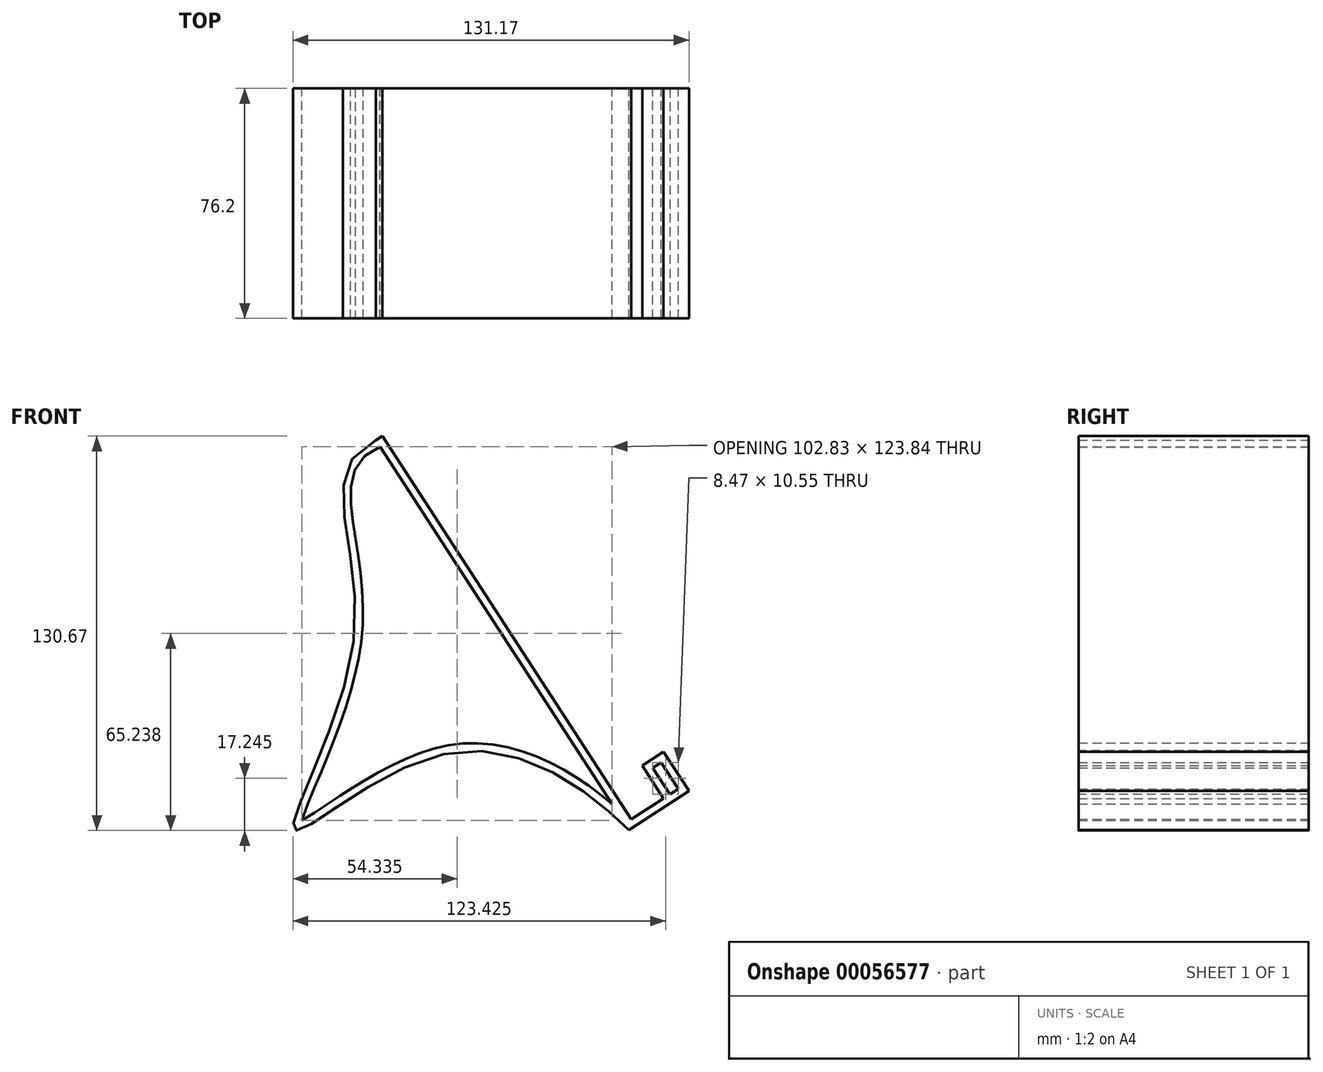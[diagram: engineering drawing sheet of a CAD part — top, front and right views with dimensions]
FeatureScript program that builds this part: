
annotation { "Feature Type Name" : "Feature", "Feature Type Description" : "" }
export const myFeature = defineFeature(function(context is Context, id is Id, definition is map)
    precondition{}
    {
        {
            var Q0;
            Q0=qCreatedBy(makeId("Front.planeOp"),FACE);
            var sketch = newSketch(context, id + "F0", { "sketchPlane" : qUnion([Q0])});
            skLineSegment(sketch, "E0.bottom", {"start": v(0, 0) * mm, "end": v(80.32, 0) * mm, "construction": true});
            skLineSegment(sketch, "E0.top", {"start": v(0, -127) * mm, "end": v(80.32, -127) * mm, "construction": true});
            skLineSegment(sketch, "E0.left", {"start": v(0, 0) * mm, "end": v(0, -127) * mm, "construction": true});
            skLineSegment(sketch, "E0.right", {"start": v(80.32, 0) * mm, "end": v(80.32, -127) * mm, "construction": true});
            skLineSegment(sketch, "E1", {"start": v(-12.8, 0) * mm, "end": v(69.67, -127) * mm});
            skLineSegment(sketch, "E2", {"start": v(69.67, -127) * mm, "end": v(80.32, -120.08) * mm});
            skLineSegment(sketch, "E3", {"start": v(80.32, -120.08) * mm, "end": v(73.27, -109.22) * mm});
            skLineSegment(sketch, "E4", {"start": v(-12.8, 0) * mm, "end": v(-14.93, -1.38) * mm});
            skLineSegment(sketch, "E5", {"start": v(-14.93, -1.38) * mm, "end": v(68.93, -130.51) * mm});
            skLineSegment(sketch, "E6", {"start": v(68.93, -130.51) * mm, "end": v(88.76, -117.63) * mm});
            skLineSegment(sketch, "E7", {"start": v(88.76, -117.63) * mm, "end": v(80.32, -104.64) * mm});
            skLineSegment(sketch, "E8", {"start": v(80.32, -104.64) * mm, "end": v(73.27, -109.22) * mm});
            skPoint(sketch, "E9.3.internal.snap0", {"position": v(0, -63.5) * mm});
            skFitSpline(sketch, "E9", {"points": [v(68.93, -130.51) * mm, v(10.64, -104.78) * mm, v(-41.93, -130.51) * mm, v(-21.9, -63.5) * mm, v(-14.93, -1.38) * mm], "startDerivative": vector(-127.8, 127.82) * mm, "endDerivative": vector(251.96, 110.75) * mm});
            skSolve(sketch);
        }
        {
            var Q0;
            Q0=makeQuery(id+"F0.imprint","IMPRINT",FACE,{"disambiguationData":[TD([[makeQuery(id+"F0.imprint","IMPRINT",EDGE,{"derivedFrom":sQuery(id+"F0.wireOp",EDGE,"E1")}),-1.0]])]});
            var Q1;
            Q1=makeQuery(id+"F0.imprint","IMPRINT",FACE,{"disambiguationData":[TD([[makeQuery(id+"F0.imprint","IMPRINT",EDGE,{"derivedFrom":sQuery(id+"F0.wireOp",EDGE,"E5")}),-1.0]])]});
            extrude(context, id + "F1", {"entities" : qUnion([Q0, Q1]), "depth" : 76.2 * mm});
        }
        {
            var Q0;
            Q0=makeQuery(id+"F1.opExtrude","CAP_FACE",FACE,{"disambiguationData":[OSD([sQuery(id+"F0.wireOp",EDGE,"E1"),sQuery(id+"F0.wireOp",EDGE,"E2"),sQuery(id+"F0.wireOp",EDGE,"E3"),sQuery(id+"F0.wireOp",EDGE,"E4"),sQuery(id+"F0.wireOp",EDGE,"E6"),sQuery(id+"F0.wireOp",EDGE,"E7"),sQuery(id+"F0.wireOp",EDGE,"E8"),sQuery(id+"F0.wireOp",EDGE,"E9")])],"isStart":true});
            var Q1;
            Q1=makeQuery(id+"F1.opExtrude","CAP_FACE",FACE,{"disambiguationData":[OSD([sQuery(id+"F0.wireOp",EDGE,"E1"),sQuery(id+"F0.wireOp",EDGE,"E2"),sQuery(id+"F0.wireOp",EDGE,"E3"),sQuery(id+"F0.wireOp",EDGE,"E4"),sQuery(id+"F0.wireOp",EDGE,"E6"),sQuery(id+"F0.wireOp",EDGE,"E7"),sQuery(id+"F0.wireOp",EDGE,"E8"),sQuery(id+"F0.wireOp",EDGE,"E9")])],"isStart":false});
            shell(context, id + "F2", {"entities" : qUnion([Q0, Q1]), "thickness" : 2.54 * mm});
        }
    });
